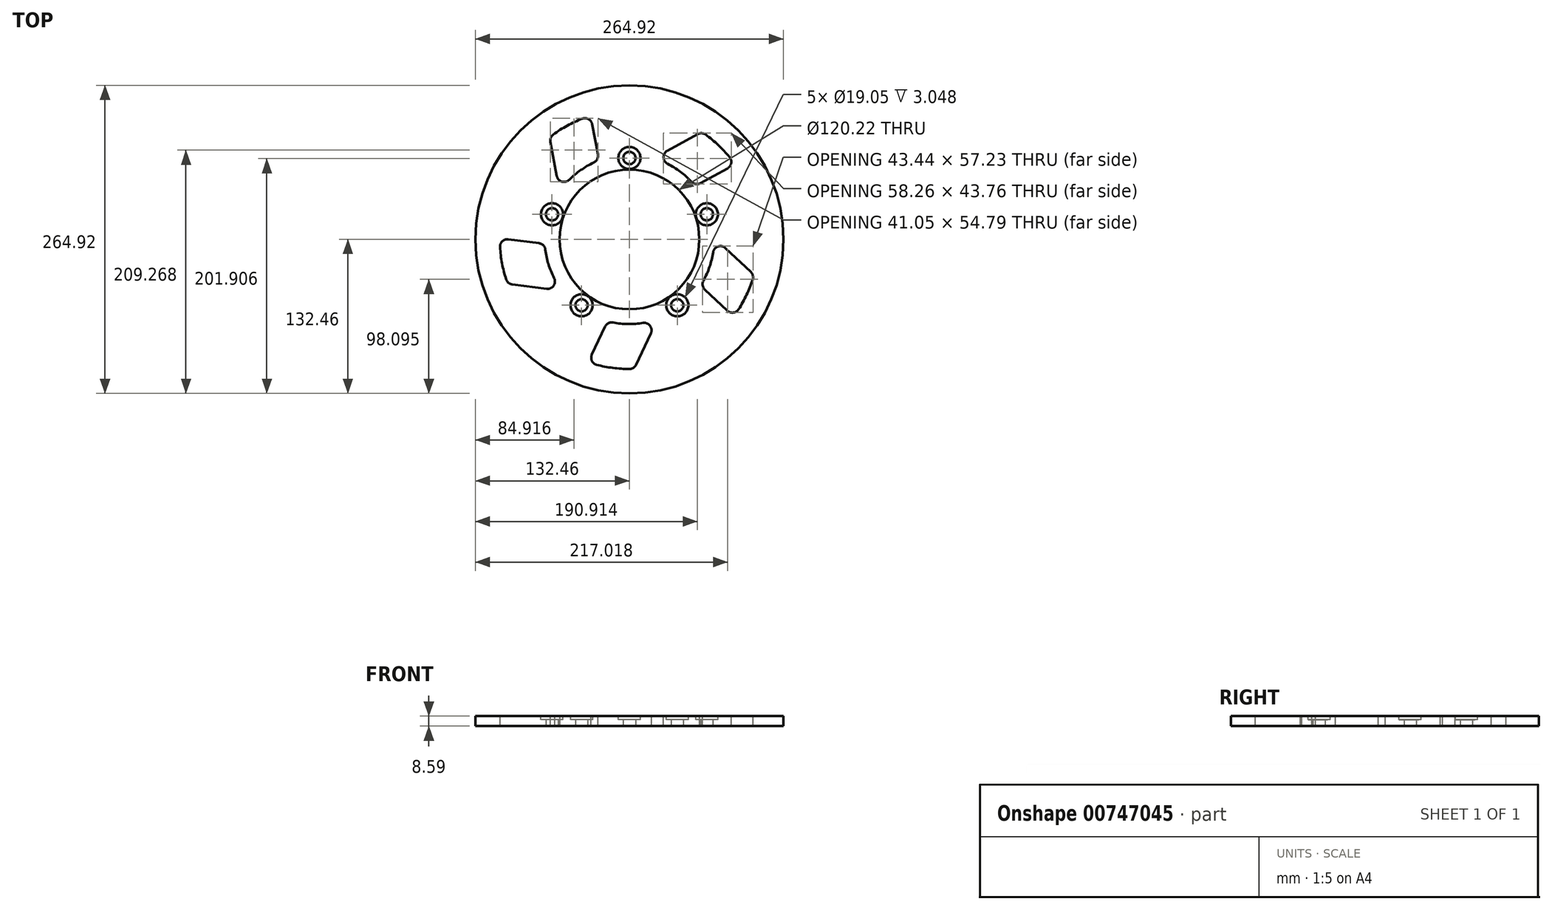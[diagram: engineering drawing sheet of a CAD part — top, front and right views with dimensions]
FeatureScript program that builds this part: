
annotation { "Feature Type Name" : "Feature", "Feature Type Description" : "" }
export const myFeature = defineFeature(function(context is Context, id is Id, definition is map)
    precondition{}
    {
        {
            var Q0;
            Q0=qCreatedBy(makeId("Top.planeOp"),FACE);
            var sketch = newSketch(context, id + "F0", { "sketchPlane" : qUnion([Q0])});
            skCircle(sketch, "E0", {"center": v(0, 0) * mm, "radius": 60.1 * mm});
            skCircle(sketch, "E1", {"center": v(0, 69.99) * mm, "radius": 5.28 * mm});
            skCircle(sketch, "E2.1.0", {"center": v(-66.56, 21.63) * mm, "radius": 5.28 * mm});
            skCircle(sketch, "E2.2.0", {"center": v(-41.14, -56.62) * mm, "radius": 5.28 * mm});
            skCircle(sketch, "E2.3.0", {"center": v(41.14, -56.62) * mm, "radius": 5.28 * mm});
            skCircle(sketch, "E2.4.0", {"center": v(66.56, 21.63) * mm, "radius": 5.28 * mm});
            skCircle(sketch, "E3", {"center": v(0, 69.99) * mm, "radius": 9.53 * mm});
            skCircle(sketch, "E4.1.0", {"center": v(-66.56, 21.63) * mm, "radius": 9.53 * mm});
            skCircle(sketch, "E4.2.0", {"center": v(-41.14, -56.62) * mm, "radius": 9.53 * mm});
            skCircle(sketch, "E4.3.0", {"center": v(41.14, -56.62) * mm, "radius": 9.53 * mm});
            skCircle(sketch, "E4.4.0", {"center": v(66.56, 21.63) * mm, "radius": 9.53 * mm});
            skCircle(sketch, "E5", {"center": v(0, 0) * mm, "radius": 124.14 * mm});
            skCircle(sketch, "E6", {"center": v(0, 0) * mm, "radius": 132.46 * mm});
            skSolve(sketch);
        }
        {
            var Q0;
            Q0=makeQuery(id+"F0.imprint","IMPRINT",FACE,{"disambiguationData":[TD([[makeQuery(id+"F0.imprint","IMPRINT",EDGE,{"derivedFrom":sQuery(id+"F0.wireOp",EDGE,"E0")}),-1.0]])]});
            var Q1;
            Q1=makeQuery(id+"F0.imprint","IMPRINT",FACE,{"disambiguationData":[TD([[makeQuery(id+"F0.imprint","IMPRINT",EDGE,{"derivedFrom":sQuery(id+"F0.wireOp",EDGE,"E1")}),-1.0]])]});
            var Q2;
            Q2=makeQuery(id+"F0.imprint","IMPRINT",FACE,{"disambiguationData":[TD([[makeQuery(id+"F0.imprint","IMPRINT",EDGE,{"derivedFrom":sQuery(id+"F0.wireOp",EDGE,"E2.4.0")}),-1.0]])]});
            var Q3;
            Q3=makeQuery(id+"F0.imprint","IMPRINT",FACE,{"disambiguationData":[TD([[makeQuery(id+"F0.imprint","IMPRINT",EDGE,{"derivedFrom":sQuery(id+"F0.wireOp",EDGE,"E2.3.0")}),-1.0]])]});
            var Q4;
            Q4=makeQuery(id+"F0.imprint","IMPRINT",FACE,{"disambiguationData":[TD([[makeQuery(id+"F0.imprint","IMPRINT",EDGE,{"derivedFrom":sQuery(id+"F0.wireOp",EDGE,"E2.2.0")}),-1.0]])]});
            var Q5;
            Q5=makeQuery(id+"F0.imprint","IMPRINT",FACE,{"disambiguationData":[TD([[makeQuery(id+"F0.imprint","IMPRINT",EDGE,{"derivedFrom":sQuery(id+"F0.wireOp",EDGE,"E2.1.0")}),-1.0]])]});
            var Q6;
            Q6=makeQuery(id+"F0.imprint","IMPRINT",FACE,{"disambiguationData":[TD([[makeQuery(id+"F0.imprint","IMPRINT",EDGE,{"derivedFrom":sQuery(id+"F0.wireOp",EDGE,"E5")}),-1.0]])]});
            extrude(context, id + "F1", {"entities" : qUnion([Q0, Q1, Q2, Q3, Q4, Q5, Q6]), "depth" : 8.6 * mm, "offsetDistance" : 25.4 * mm});
        }
        {
            var Q0;
            Q0=makeQuery(id+"F1.opExtrude","CAP_FACE",FACE,{"disambiguationData":[OSD([sQuery(id+"F0.wireOp",EDGE,"E0"),sQuery(id+"F0.wireOp",EDGE,"E1"),sQuery(id+"F0.wireOp",EDGE,"E2.1.0"),sQuery(id+"F0.wireOp",EDGE,"E2.2.0"),sQuery(id+"F0.wireOp",EDGE,"E2.3.0"),sQuery(id+"F0.wireOp",EDGE,"E2.4.0"),sQuery(id+"F0.wireOp",EDGE,"E6")])],"isStart":false});
            var sketch = newSketch(context, id + "F2", { "sketchPlane" : qUnion([Q0])});
            skCircle(sketch, "E7", {"center": v(0, 69.99) * mm, "radius": 9.53 * mm});
            skCircle(sketch, "E8.1.0", {"center": v(-66.56, 21.63) * mm, "radius": 9.53 * mm});
            skCircle(sketch, "E8.2.0", {"center": v(-41.14, -56.62) * mm, "radius": 9.53 * mm});
            skCircle(sketch, "E8.3.0", {"center": v(41.14, -56.62) * mm, "radius": 9.53 * mm});
            skCircle(sketch, "E8.4.0", {"center": v(66.56, 21.63) * mm, "radius": 9.53 * mm});
            skPoint(sketch, "E8.center", {"position": v(0, 0) * mm});
            skSolve(sketch);
        }
        {
            var Q0;
            Q0=makeQuery(id+"F2.imprint","IMPRINT",FACE,{"disambiguationData":[TD([[makeQuery(id+"F2.imprint","IMPRINT",EDGE,{"derivedFrom":sQuery(id+"F2.wireOp",EDGE,"E8.1.0")}),1.0]])]});
            var Q1;
            Q1=makeQuery(id+"F2.imprint","IMPRINT",FACE,{"disambiguationData":[TD([[makeQuery(id+"F2.imprint","IMPRINT",EDGE,{"derivedFrom":sQuery(id+"F2.wireOp",EDGE,"E7")}),1.0]])]});
            var Q2;
            Q2=makeQuery(id+"F2.imprint","IMPRINT",FACE,{"disambiguationData":[TD([[makeQuery(id+"F2.imprint","IMPRINT",EDGE,{"derivedFrom":sQuery(id+"F2.wireOp",EDGE,"E8.4.0")}),1.0]])]});
            var Q3;
            Q3=makeQuery(id+"F2.imprint","IMPRINT",FACE,{"disambiguationData":[TD([[makeQuery(id+"F2.imprint","IMPRINT",EDGE,{"derivedFrom":sQuery(id+"F2.wireOp",EDGE,"E8.3.0")}),1.0]])]});
            var Q4;
            Q4=makeQuery(id+"F2.imprint","IMPRINT",FACE,{"disambiguationData":[TD([[makeQuery(id+"F2.imprint","IMPRINT",EDGE,{"derivedFrom":sQuery(id+"F2.wireOp",EDGE,"E8.2.0")}),1.0]])]});
            extrude(context, id + "F3", {"entities" : qUnion([Q0, Q1, Q2, Q3, Q4]), "operationType" : NewBodyOperationType.REMOVE, "oppositeDirection" : true, "depth" : 3.05 * mm, "offsetDistance" : 25.4 * mm});
        }
        {
            var Q0;
            Q0=makeQuery(id+"F1.opExtrude","CAP_FACE",FACE,{"disambiguationData":[OSD([sQuery(id+"F0.wireOp",EDGE,"E0"),sQuery(id+"F0.wireOp",EDGE,"E1"),sQuery(id+"F0.wireOp",EDGE,"E2.1.0"),sQuery(id+"F0.wireOp",EDGE,"E2.2.0"),sQuery(id+"F0.wireOp",EDGE,"E2.3.0"),sQuery(id+"F0.wireOp",EDGE,"E2.4.0"),sQuery(id+"F0.wireOp",EDGE,"E6")])],"isStart":false});
            var sketch = newSketch(context, id + "F4", { "sketchPlane" : qUnion([Q0])});
            skArc(sketch, "E9", {"start": v(-30.69, 66.03) * mm, "mid": v(-41.84, 59.59) * mm, "end": v(-51.68, 51.29) * mm});
            skCircle(sketch, "E10", {"center": v(0, 0) * mm, "radius": 124.14 * mm});
            skArc(sketch, "E11", {"start": v(-40.62, 103.78) * mm, "mid": v(-53.47, 97.78) * mm, "end": v(-65.46, 90.2) * mm});
            skLineSegment(sketch, "E12", {"start": v(-62.42, 54.58) * mm, "end": v(-67.97, 83.87) * mm});
            skLineSegment(sketch, "E13.0", {"start": v(-27.13, 72.96) * mm, "end": v(-32.06, 99.05) * mm});
            skPoint(sketch, "E14.visualSharp", {"position": v(-68.7, 87.75) * mm});
            skArc(sketch, "E14.filletArc", {"start": v(-65.46, 90.2) * mm, "mid": v(-67.63, 87.4) * mm, "end": v(-67.97, 83.87) * mm});
            skPoint(sketch, "E15.visualSharp", {"position": v(-33.44, 106.3) * mm});
            skArc(sketch, "E15.filletArc", {"start": v(-32.06, 99.05) * mm, "mid": v(-35.23, 103.42) * mm, "end": v(-40.62, 103.78) * mm});
            skPoint(sketch, "E16.visualSharp", {"position": v(-26.18, 67.94) * mm});
            skArc(sketch, "E16.filletArc", {"start": v(-30.69, 66.03) * mm, "mid": v(-27.72, 68.88) * mm, "end": v(-27.13, 72.96) * mm});
            skPoint(sketch, "E17.visualSharp", {"position": v(-59.92, 41.36) * mm});
            skArc(sketch, "E17.filletArc", {"start": v(-62.42, 54.58) * mm, "mid": v(-58.04, 49.7) * mm, "end": v(-51.68, 51.29) * mm});
            skLineSegment(sketch, "E18.1.0", {"start": v(-77.78, -3.25) * mm, "end": v(-104.1, 0.11) * mm});
            skArc(sketch, "E18.1.1", {"start": v(-104.1, 0.11) * mm, "mid": v(-109.24, -1.54) * mm, "end": v(-111.25, -6.56) * mm});
            skArc(sketch, "E18.1.2", {"start": v(-111.25, -6.56) * mm, "mid": v(-109.51, -20.64) * mm, "end": v(-106, -34.38) * mm});
            skArc(sketch, "E18.1.3", {"start": v(-106, -34.38) * mm, "mid": v(-104.02, -37.31) * mm, "end": v(-100.77, -38.72) * mm});
            skLineSegment(sketch, "E18.1.4", {"start": v(-71.2, -42.5) * mm, "end": v(-100.77, -38.72) * mm});
            skArc(sketch, "E18.1.5", {"start": v(-71.2, -42.5) * mm, "mid": v(-65.2, -39.85) * mm, "end": v(-64.75, -33.3) * mm});
            skArc(sketch, "E18.1.6", {"start": v(-72.28, -8.78) * mm, "mid": v(-69.6, -21.38) * mm, "end": v(-64.75, -33.3) * mm});
            skArc(sketch, "E18.1.7", {"start": v(-72.28, -8.78) * mm, "mid": v(-74.08, -5.07) * mm, "end": v(-77.78, -3.25) * mm});
            skLineSegment(sketch, "E18.2.0", {"start": v(-20.94, -74.97) * mm, "end": v(-32.28, -98.97) * mm});
            skArc(sketch, "E18.2.1", {"start": v(-32.28, -98.97) * mm, "mid": v(-32.29, -104.38) * mm, "end": v(-28.14, -107.83) * mm});
            skArc(sketch, "E18.2.2", {"start": v(-28.14, -107.83) * mm, "mid": v(-14.21, -110.53) * mm, "end": v(-0.06, -111.44) * mm});
            skArc(sketch, "E18.2.3", {"start": v(-0.06, -111.44) * mm, "mid": v(3.34, -110.46) * mm, "end": v(5.69, -107.8) * mm});
            skLineSegment(sketch, "E18.2.4", {"start": v(18.42, -80.85) * mm, "end": v(5.69, -107.8) * mm});
            skArc(sketch, "E18.2.5", {"start": v(18.42, -80.85) * mm, "mid": v(17.75, -74.32) * mm, "end": v(11.66, -71.87) * mm});
            skArc(sketch, "E18.2.6", {"start": v(-13.98, -71.45) * mm, "mid": v(-1.18, -72.8) * mm, "end": v(11.66, -71.87) * mm});
            skArc(sketch, "E18.2.7", {"start": v(-13.98, -71.45) * mm, "mid": v(-18.07, -72.02) * mm, "end": v(-20.94, -74.97) * mm});
            skLineSegment(sketch, "E18.3.0", {"start": v(64.83, -43.08) * mm, "end": v(84.16, -61.28) * mm});
            skArc(sketch, "E18.3.1", {"start": v(84.16, -61.28) * mm, "mid": v(89.29, -62.96) * mm, "end": v(93.86, -60.08) * mm});
            skArc(sketch, "E18.3.2", {"start": v(93.86, -60.08) * mm, "mid": v(100.73, -47.67) * mm, "end": v(105.97, -34.5) * mm});
            skArc(sketch, "E18.3.3", {"start": v(105.97, -34.5) * mm, "mid": v(106.08, -30.95) * mm, "end": v(104.29, -27.9) * mm});
            skLineSegment(sketch, "E18.3.4", {"start": v(82.58, -7.47) * mm, "end": v(104.29, -27.9) * mm});
            skArc(sketch, "E18.3.5", {"start": v(82.58, -7.47) * mm, "mid": v(76.17, -6.08) * mm, "end": v(71.96, -11.12) * mm});
            skArc(sketch, "E18.3.6", {"start": v(63.64, -35.38) * mm, "mid": v(68.87, -23.62) * mm, "end": v(71.96, -11.12) * mm});
            skArc(sketch, "E18.3.7", {"start": v(63.64, -35.38) * mm, "mid": v(62.91, -39.44) * mm, "end": v(64.83, -43.08) * mm});
            skLineSegment(sketch, "E18.4.0", {"start": v(61.01, 48.35) * mm, "end": v(84.29, 61.1) * mm});
            skArc(sketch, "E18.4.1", {"start": v(84.29, 61.1) * mm, "mid": v(87.47, 65.46) * mm, "end": v(86.15, 70.7) * mm});
            skArc(sketch, "E18.4.2", {"start": v(86.15, 70.7) * mm, "mid": v(76.47, 81.07) * mm, "end": v(65.55, 90.13) * mm});
            skArc(sketch, "E18.4.3", {"start": v(65.55, 90.13) * mm, "mid": v(62.22, 91.33) * mm, "end": v(58.76, 90.56) * mm});
            skLineSegment(sketch, "E18.4.4", {"start": v(32.62, 76.24) * mm, "end": v(58.76, 90.56) * mm});
            skArc(sketch, "E18.4.5", {"start": v(32.62, 76.24) * mm, "mid": v(29.32, 70.56) * mm, "end": v(32.8, 65) * mm});
            skArc(sketch, "E18.4.6", {"start": v(53.31, 49.6) * mm, "mid": v(43.74, 58.2) * mm, "end": v(32.8, 65) * mm});
            skArc(sketch, "E18.4.7", {"start": v(53.31, 49.6) * mm, "mid": v(56.95, 47.65) * mm, "end": v(61.01, 48.35) * mm});
            skSolve(sketch);
        }
        {
            var Q0;
            Q0=makeQuery(id+"F4.imprint","IMPRINT",FACE,{"disambiguationData":[TD([[makeQuery(id+"F4.imprint","IMPRINT",EDGE,{"derivedFrom":sQuery(id+"F4.wireOp",EDGE,"E9")}),-1.0]])]});
            var Q1;
            Q1=makeQuery(id+"F4.imprint","IMPRINT",FACE,{"disambiguationData":[TD([[makeQuery(id+"F4.imprint","IMPRINT",EDGE,{"derivedFrom":sQuery(id+"F4.wireOp",EDGE,"E18.4.0")}),1.0]])]});
            var Q2;
            Q2=makeQuery(id+"F4.imprint","IMPRINT",FACE,{"disambiguationData":[TD([[makeQuery(id+"F4.imprint","IMPRINT",EDGE,{"derivedFrom":sQuery(id+"F4.wireOp",EDGE,"E18.3.0")}),1.0]])]});
            var Q3;
            Q3=makeQuery(id+"F4.imprint","IMPRINT",FACE,{"disambiguationData":[TD([[makeQuery(id+"F4.imprint","IMPRINT",EDGE,{"derivedFrom":sQuery(id+"F4.wireOp",EDGE,"E18.1.0")}),1.0]])]});
            var Q4;
            Q4=makeQuery(id+"F4.imprint","IMPRINT",FACE,{"disambiguationData":[TD([[makeQuery(id+"F4.imprint","IMPRINT",EDGE,{"derivedFrom":sQuery(id+"F4.wireOp",EDGE,"E18.2.0")}),1.0]])]});
            extrude(context, id + "F5", {"entities" : qUnion([Q0, Q1, Q2, Q3, Q4]), "operationType" : NewBodyOperationType.REMOVE, "endBound" : BoundingType.THROUGH_ALL, "oppositeDirection" : true, "depth" : 25.4 * mm, "offsetDistance" : 25.4 * mm});
        }
    });
